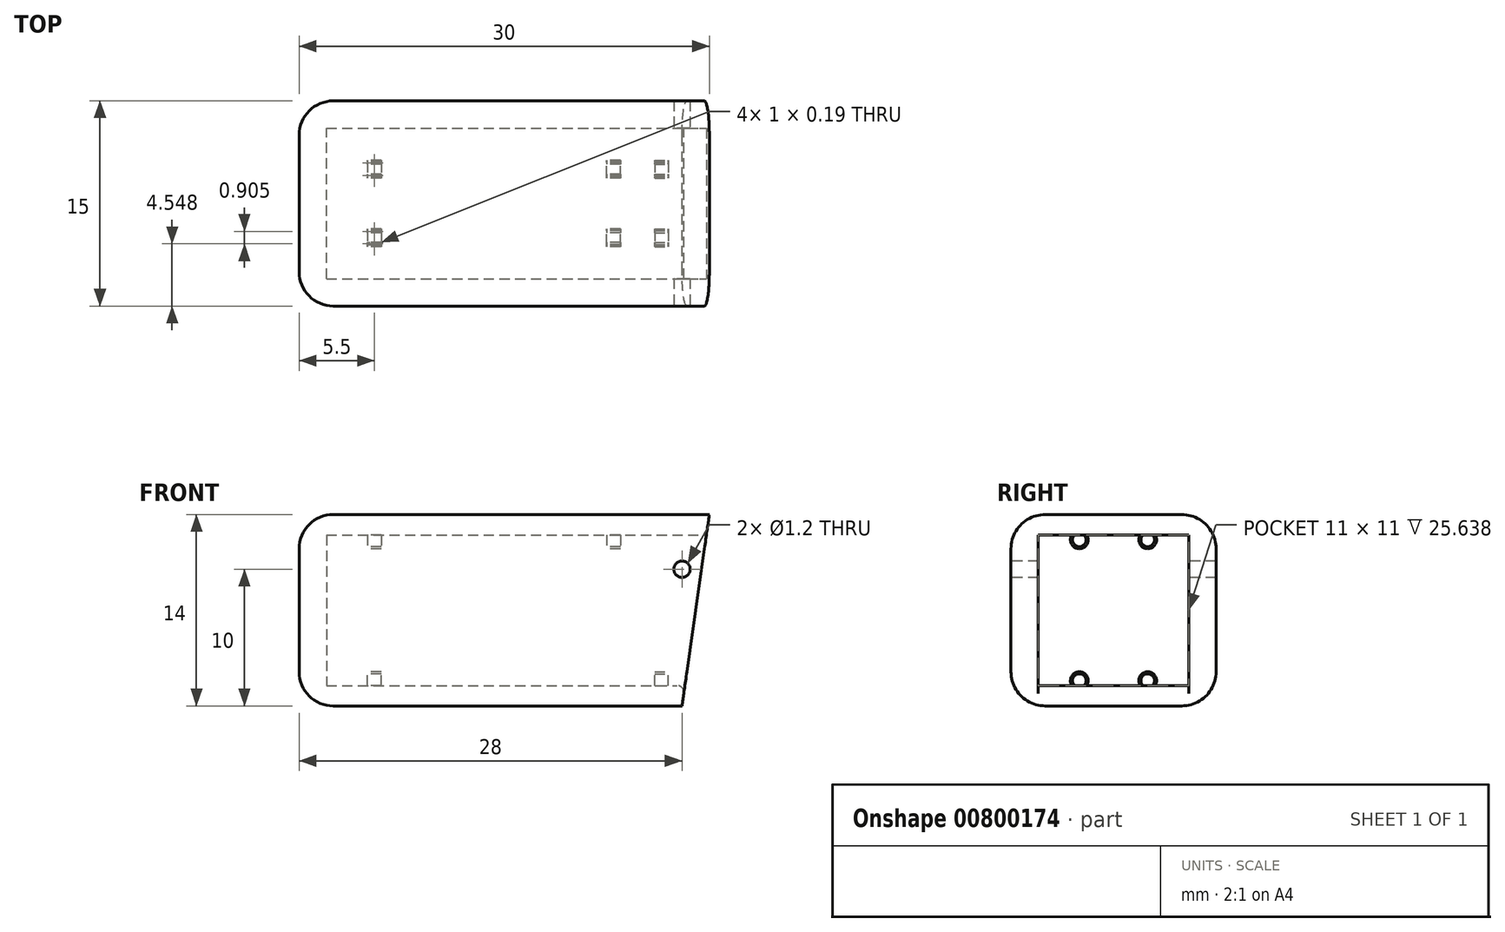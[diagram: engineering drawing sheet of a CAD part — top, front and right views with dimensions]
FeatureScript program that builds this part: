
annotation { "Feature Type Name" : "Feature", "Feature Type Description" : "" }
export const myFeature = defineFeature(function(context is Context, id is Id, definition is map)
    precondition{}
    {
        {
            var Q0;
            Q0=qCreatedBy(makeId("Front.planeOp"),FACE);
            var sketch = newSketch(context, id + "F0", { "sketchPlane" : qUnion([Q0])});
            skLineSegment(sketch, "E0.bottom", {"start": v(-15, 7) * mm, "end": v(15, 7) * mm});
            skLineSegment(sketch, "E0.top", {"start": v(-15, -7) * mm, "end": v(15, -7) * mm});
            skLineSegment(sketch, "E0.left", {"start": v(-15, 7) * mm, "end": v(-15, -7) * mm});
            skLineSegment(sketch, "E0.right", {"start": v(15, 7) * mm, "end": v(15, -7) * mm});
            skPoint(sketch, "E0.middle", {"position": v(0, 0) * mm});
            skSolve(sketch);
        }
        {
            var Q0;
            Q0=makeQuery(id+"F0.imprint","IMPRINT",FACE,{"disambiguationData":[TD([[makeQuery(id+"F0.imprint","IMPRINT",EDGE,{"derivedFrom":sQuery(id+"F0.wireOp",EDGE,"E0.bottom")}),-1.0]])]});
            extrude(context, id + "F1", {"entities" : qUnion([Q0]), "depth" : 15 * mm, "offsetDistance" : 25 * mm});
        }
        {
            var Q0;
            Q0=makeQuery(id+"F1.opExtrude","SWEPT_FACE",FACE,{"disambiguationData":[OSD([sQuery(id+"F0.wireOp",EDGE,"E0.right")])]});
            var sketch = newSketch(context, id + "F2", { "sketchPlane" : qUnion([Q0])});
            skLineSegment(sketch, "E1.bottom", {"start": v(-13, 5.5) * mm, "end": v(-2, 5.5) * mm});
            skLineSegment(sketch, "E1.top", {"start": v(-13, -5.5) * mm, "end": v(-2, -5.5) * mm});
            skLineSegment(sketch, "E1.left", {"start": v(-13, 5.5) * mm, "end": v(-13, -5.5) * mm});
            skLineSegment(sketch, "E1.right", {"start": v(-2, 5.5) * mm, "end": v(-2, -5.5) * mm});
            skPoint(sketch, "E1.middle", {"position": v(-7.5, 0) * mm});
            skSolve(sketch);
        }
        {
            var Q0;
            Q0=makeQuery(id+"F2.imprint","IMPRINT",FACE,{"disambiguationData":[TD([[makeQuery(id+"F2.imprint","IMPRINT",EDGE,{"derivedFrom":sQuery(id+"F2.wireOp",EDGE,"E1.bottom")}),-1.0]])]});
            extrude(context, id + "F3", {"entities" : qUnion([Q0]), "operationType" : NewBodyOperationType.REMOVE, "oppositeDirection" : true, "depth" : 28 * mm, "offsetDistance" : 25 * mm});
        }
        {
            var Q0;
            Q0=qCreatedBy(makeId("Right.planeOp"),FACE);
            cPlane(context, id + "F4", {"entities" : qUnion([Q0]), "cplaneType" : CPlaneType.OFFSET, "offset" : 12 * mm, "width" : 150 * mm, "height" : 150 * mm});
        }
        {
            var Q0;
            Q0=qCreatedBy(id+"F4.planeOp",FACE);
            var sketch = newSketch(context, id + "F5", { "sketchPlane" : qUnion([Q0])});
            skCircle(sketch, "E2", {"center": v(-10, -5.15) * mm, "radius": 0.65 * mm});
            skCircle(sketch, "E3", {"center": v(-10, -5.15) * mm, "radius": 0.5 * mm});
            skCircle(sketch, "E4", {"center": v(-5, -5.15) * mm, "radius": 0.65 * mm});
            skCircle(sketch, "E5", {"center": v(-5, -5.15) * mm, "radius": 0.5 * mm});
            skSolve(sketch);
        }
        {
            var Q0;
            Q0 = qSketchRegion(id + "F5", true);
            extrude(context, id + "F6", {"entities" : qUnion([Q0]), "operationType" : NewBodyOperationType.ADD, "oppositeDirection" : true, "depth" : 1 * mm, "offsetDistance" : 25 * mm});
        }
        {
            var Q0;
            Q0=makeQuery(id+"F1.opExtrude","CAP_FACE",FACE,{"disambiguationData":[OSD([sQuery(id+"F0.wireOp",EDGE,"E0.bottom"),sQuery(id+"F0.wireOp",EDGE,"E0.top"),sQuery(id+"F0.wireOp",EDGE,"E0.left"),sQuery(id+"F0.wireOp",EDGE,"E0.right")])],"isStart":true});
            var sketch = newSketch(context, id + "F7", { "sketchPlane" : qUnion([Q0])});
            skLineSegment(sketch, "E6", {"start": v(-15, 7) * mm, "end": v(-13, -7) * mm});
            skSolve(sketch);
        }
        {
            var Q0;
            {var subQ0=sQuery(id+"F7.wireOp",EDGE,"E6");Q0=makeQuery(id+"F7.imprint","IMPRINT",FACE,{"disambiguationData":[TD([[makeQuery(id+"F7.imprint","IMPRINT",EDGE,{"derivedFrom":subQ0}),-1.0]])]});}
            extrude(context, id + "F8", {"entities" : qUnion([Q0]), "operationType" : NewBodyOperationType.REMOVE, "oppositeDirection" : true, "depth" : 25 * mm, "offsetDistance" : 25 * mm});
        }
        {
            var Q0;
            Q0=makeQuery(id+"F1.opExtrude","CAP_EDGE",EDGE,{"disambiguationData":[OSD([sQuery(id+"F0.wireOp",EDGE,"E0.bottom")])],"isStart":true});
            var Q1;
            Q1=makeQuery(id+"F1.opExtrude","CAP_EDGE",EDGE,{"disambiguationData":[OSD([sQuery(id+"F0.wireOp",EDGE,"E0.bottom")])],"isStart":false});
            var Q2;
            Q2=makeQuery(id+"F1.opExtrude","CAP_EDGE",EDGE,{"disambiguationData":[OSD([sQuery(id+"F0.wireOp",EDGE,"E0.top")])],"isStart":true});
            var Q3;
            Q3=makeQuery(id+"F1.opExtrude","SWEPT_FACE",FACE,{"disambiguationData":[OSD([sQuery(id+"F0.wireOp",EDGE,"E0.left")])]});
            var Q4;
            Q4=makeQuery(id+"F1.opExtrude","CAP_EDGE",EDGE,{"disambiguationData":[OSD([sQuery(id+"F0.wireOp",EDGE,"E0.top")])],"isStart":false});
            fillet(context, id + "F9", {"entities" : qUnion([Q0, Q1, Q2, Q3, Q4]), "radius" : 2.5 * mm, "tangentPropagation" : true, "allowEdgeOverflow" : false});
        }
        {
            var Q0;
            Q0=makeQuery(id+"F1.opExtrude","CAP_FACE",FACE,{"disambiguationData":[OSD([sQuery(id+"F0.wireOp",EDGE,"E0.bottom"),sQuery(id+"F0.wireOp",EDGE,"E0.top"),sQuery(id+"F0.wireOp",EDGE,"E0.left"),sQuery(id+"F0.wireOp",EDGE,"E0.right")])],"isStart":false});
            var sketch = newSketch(context, id + "F10", { "sketchPlane" : qUnion([Q0])});
            skCircle(sketch, "E7", {"center": v(13, 3) * mm, "radius": 0.6 * mm});
            skSolve(sketch);
        }
        {
            var Q0;
            Q0=makeQuery(id+"F10.imprint","IMPRINT",FACE,{"disambiguationData":[TD([[makeQuery(id+"F10.imprint","IMPRINT",EDGE,{"derivedFrom":sQuery(id+"F10.wireOp",EDGE,"E7")}),1.0]])]});
            extrude(context, id + "F11", {"entities" : qUnion([Q0]), "operationType" : NewBodyOperationType.REMOVE, "oppositeDirection" : true, "depth" : 20 * mm, "offsetDistance" : 25 * mm});
        }
        {
            var Q0;
            Q0=qCreatedBy(makeId("Right.planeOp"),FACE);
            cPlane(context, id + "F12", {"entities" : qUnion([Q0]), "cplaneType" : CPlaneType.OFFSET, "offset" : 10 * mm, "oppositeDirection" : true, "width" : 150 * mm, "height" : 150 * mm});
        }
        {
            var Q0;
            Q0=qCreatedBy(id+"F12.planeOp",FACE);
            var sketch = newSketch(context, id + "F13", { "sketchPlane" : qUnion([Q0])});
            skCircle(sketch, "E8", {"center": v(-10, -5.15) * mm, "radius": 0.65 * mm});
            skCircle(sketch, "E9", {"center": v(-10, -5.15) * mm, "radius": 0.5 * mm});
            skCircle(sketch, "E10", {"center": v(-5, -5.15) * mm, "radius": 0.65 * mm});
            skCircle(sketch, "E11", {"center": v(-5, -5.15) * mm, "radius": 0.5 * mm});
            skSolve(sketch);
        }
        {
            var Q0;
            Q0 = qSketchRegion(id + "F13", true);
            extrude(context, id + "F14", {"entities" : qUnion([Q0]), "operationType" : NewBodyOperationType.ADD, "depth" : 1 * mm, "offsetDistance" : 25 * mm});
        }
        {
            var Q0;
            Q0=makeQuery(id+"F8.boolean.opBoolean","INTERSECT",EDGE,{"derivedFrom":[makeQuery(id+"F3.boolean.opBoolean","COPY",FACE,{"derivedFrom":makeQuery(id+"F3.opExtrude","SWEPT_FACE",FACE,{"disambiguationData":[OSD([sQuery(id+"F2.wireOp",EDGE,"E1.top")])]})}),makeQuery(id+"F8.opExtrude","SWEPT_FACE",FACE,{"disambiguationData":[OSD([sQuery(id+"F7.wireOp",EDGE,"E6")])]})]});
            fillet(context, id + "F15", {"entities" : qUnion([Q0]), "radius" : 0.5 * mm, "tangentPropagation" : true, "allowEdgeOverflow" : false});
        }
        {
            var Q0;
            Q0=qCreatedBy(makeId("Right.planeOp"),FACE);
            cPlane(context, id + "F16", {"entities" : qUnion([Q0]), "cplaneType" : CPlaneType.OFFSET, "offset" : 8 * mm, "width" : 150 * mm, "height" : 150 * mm});
        }
        {
            var Q0;
            Q0=qCreatedBy(id+"F16.planeOp",FACE);
            var sketch = newSketch(context, id + "F17", { "sketchPlane" : qUnion([Q0])});
            skCircle(sketch, "E12", {"center": v(-10, 5.15) * mm, "radius": 0.65 * mm});
            skCircle(sketch, "E13", {"center": v(-10, 5.15) * mm, "radius": 0.5 * mm});
            skCircle(sketch, "E14", {"center": v(-5, 5.15) * mm, "radius": 0.65 * mm});
            skCircle(sketch, "E15", {"center": v(-5, 5.15) * mm, "radius": 0.5 * mm});
            skSolve(sketch);
        }
        {
            var Q0;
            Q0 = qSketchRegion(id + "F17", true);
            extrude(context, id + "F18", {"entities" : qUnion([Q0]), "operationType" : NewBodyOperationType.ADD, "depth" : 0.5 * mm, "offsetDistance" : 25 * mm, "hasSecondDirection" : true, "secondDirectionOppositeDirection" : true, "secondDirectionDepth" : 0.5 * mm});
        }
        {
            var Q0;
            Q0=qCreatedBy(id+"F12.planeOp",FACE);
            var sketch = newSketch(context, id + "F19", { "sketchPlane" : qUnion([Q0])});
            skCircle(sketch, "E16", {"center": v(-10, 5.15) * mm, "radius": 0.65 * mm});
            skCircle(sketch, "E17", {"center": v(-10, 5.15) * mm, "radius": 0.5 * mm});
            skCircle(sketch, "E18", {"center": v(-5, 5.15) * mm, "radius": 0.65 * mm});
            skCircle(sketch, "E19", {"center": v(-5, 5.15) * mm, "radius": 0.5 * mm});
            skSolve(sketch);
        }
        {
            var Q0;
            Q0 = qSketchRegion(id + "F19", true);
            extrude(context, id + "F20", {"entities" : qUnion([Q0]), "operationType" : NewBodyOperationType.ADD, "depth" : 1 * mm, "offsetDistance" : 25 * mm});
        }
    });
